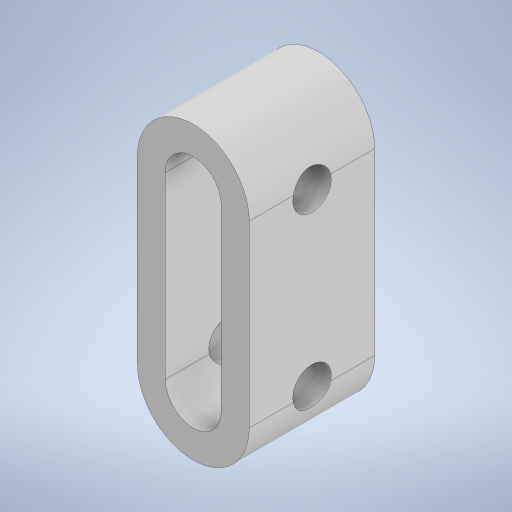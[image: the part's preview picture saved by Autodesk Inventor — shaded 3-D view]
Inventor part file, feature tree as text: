
AUTODESK INVENTOR PART (.ipt)
format: ipt  version: 2023.2 (Build 272271030, 271C)  size: 266,240 bytes
history: native  units: mm
features: extrude x2, sketch x2, plane x1, projected_geometry x1
ambient origin geometry x8: Origin, YZ Plane, XZ Plane, XY Plane, X Axis, Y Axis, Z Axis, Center Point
bodies: Solid1 (feature_tree)
feature tree (6):
  extrude  "Extrusion1"  Depth=12.5mm
  plane  "Work Plane1"
  extrude  "Extrusion2"  Depth=28.0mm TaperAngle=0.0deg
  sketch  "Sketch1"  dims[d0=40.0mm d1=12.5mm]
  sketch  "Sketch2"  dims[d2=12.5mm d3=28.0mm d4=0.0mm d5=12.5mm d6=8.6mm d8=28.0mm d9=0.0mm d10=38.0mm]
  projected_geometry  "Projected Loop1"
